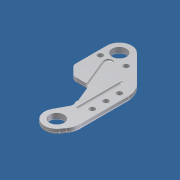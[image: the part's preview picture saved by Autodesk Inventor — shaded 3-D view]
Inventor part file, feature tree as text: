
AUTODESK INVENTOR PART (.ipt)
format: ipt  version: unknown  size: 324,096 bytes
history: native  units: in
note: dims shown in document units (in); Inventor stores cm internally (conversion verified against a paired STEP export)
features: extrude x4, sketch x4, fillet x3, other x3
ambient origin geometry x8: Origin, YZ Plane, XZ Plane, XY Plane, X Axis, Y Axis, Z Axis, Center Point
bodies: Solid1 (feature_tree), Solid2 (feature_tree), Solid3 (feature_tree), Solid4 (feature_tree)
feature tree (14):
  extrude  "Extrude1"  Depth=0.213in
  fillet  "Fillet1 (Constant)"  Radius=0.875in
  extrude  "Extrude2"  Depth=0.534in
  other  "Boolean1 (Cut)"
  fillet  "Fillet2 (Constant)"  Radius=0.1506in
  extrude  "Extrude3"  Depth=0.534in
  other  "Boolean2 (Cut)"
  extrude  "Extrude4"  Depth=0.1in
  other  "Boolean3 (Cut)"
  fillet  "Fillet3 (Constant)"  Radius=0.0669in
  sketch  "Sketch1"  dims[d0=0.745in d1=0.213in d2=0.875in]
  sketch  "Sketch2"  dims[d3=0.1877in d4=0.534in d5=0.1506in]
  sketch  "Sketch3"  dims[d6=0.1335in d7=0.534in]
  sketch  "Sketch4"  dims[d8=0.2362in d9=0.0in d10=0.1in d11=0.0669in d12=0.0in d13=0.06in d14=0.315in d15=0.315in d16=0.118in d17=0.118in d18=0.118in d19=0.118in d20=0.118in d21=0.59in d22=0.59in d23=1.0in d24=0.0in d25=0.475in d26=0.078in d27=0.0in d28=0.02in]
